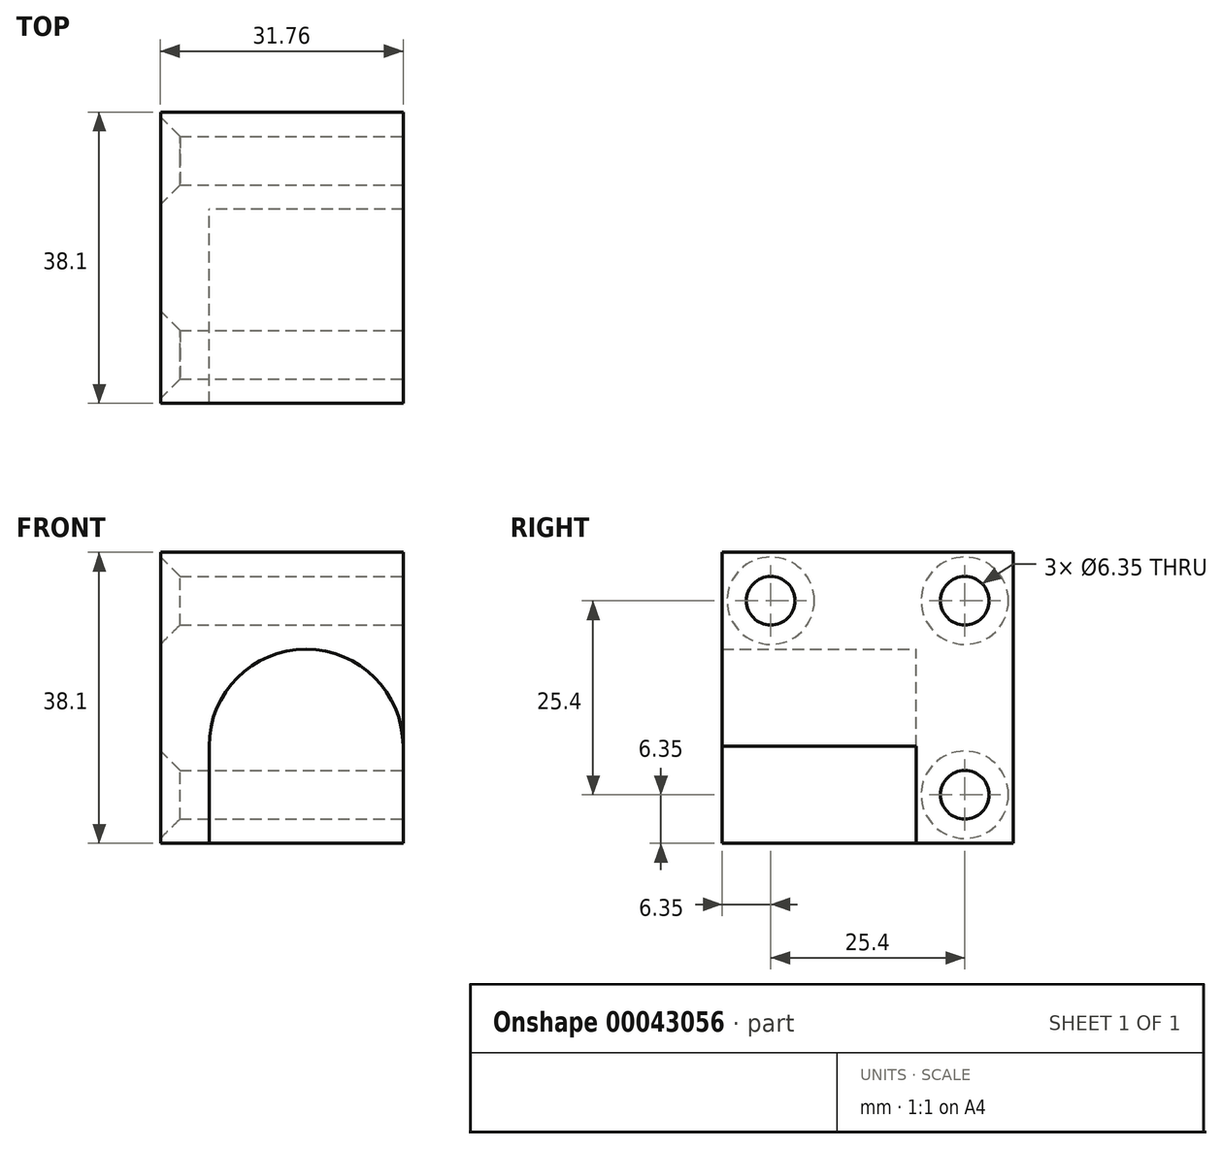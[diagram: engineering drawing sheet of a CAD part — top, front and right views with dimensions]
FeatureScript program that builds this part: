
annotation { "Feature Type Name" : "Feature", "Feature Type Description" : "" }
export const myFeature = defineFeature(function(context is Context, id is Id, definition is map)
    precondition{}
    {
        {
            var Q0;
            Q0=qCreatedBy(makeId("Front.planeOp"),FACE);
            var sketch = newSketch(context, id + "F0", { "sketchPlane" : qUnion([Q0])});
            skLineSegment(sketch, "E0.rect.bottom", {"start": v(15.88, 19.05) * mm, "end": v(-15.87, 19.05) * mm});
            skLineSegment(sketch, "E0.rect.top", {"start": v(15.87, -19.05) * mm, "end": v(-15.88, -19.05) * mm});
            skLineSegment(sketch, "E0.rect.left", {"start": v(15.87, 19.05) * mm, "end": v(15.87, -19.05) * mm});
            skLineSegment(sketch, "E0.rect.right", {"start": v(-15.88, 19.05) * mm, "end": v(-15.88, -19.05) * mm});
            skPoint(sketch, "E0.rect.middle", {"position": v(0, 0) * mm});
            skCircle(sketch, "E1", {"center": v(3.17, -6.35) * mm, "radius": 12.7 * mm});
            skLineSegment(sketch, "E2", {"start": v(-9.53, -6.35) * mm, "end": v(-9.53, -19.05) * mm});
            skSolve(sketch);
        }
        {
            var Q0;
            {var subQ4=sQuery(id+"F0.wireOp",EDGE,"E0.rect.bottom");Q0=makeQuery(id+"F0.imprint","IMPRINT",FACE,{"disambiguationData":[TD([[makeQuery(id+"F0.imprint","IMPRINT",EDGE,{"derivedFrom":subQ4}),1.0]])]});}
            extrude(context, id + "F1", {"entities" : qUnion([Q0]), "depth" : 38.1 * mm});
        }
        {
            var Q0;
            {var subQ0=sQuery(id+"F0.wireOp",EDGE,"E1");var subQ3=makeQuery(id+"F0.imprint","INTERSECT",VERTEX,{"derivedFrom":[subQ0,sQuery(id+"F0.wireOp",EDGE,"E2")]});Q0=makeQuery(id+"F0.imprint","IMPRINT",FACE,{"disambiguationData":[TD([[makeQuery(id+"F0.imprint","IMPRINT",EDGE,{"disambiguationData":[TD([[subQ3,1.0]])],"derivedFrom":subQ0}),1.0]])]});}
            var Q1;
            {var subQ1=sQuery(id+"F0.wireOp",EDGE,"E0.rect.left");var subQ3=sQuery(id+"F0.wireOp",EDGE,"E0.rect.top");var subQ5=makeQuery(id+"F0.imprint","INTERSECT",VERTEX,{"derivedFrom":[subQ3,subQ1]});Q1=makeQuery(id+"F0.imprint","IMPRINT",FACE,{"disambiguationData":[TD([[makeQuery(id+"F0.imprint","IMPRINT",EDGE,{"disambiguationData":[TD([[subQ5,-1.0]])],"derivedFrom":subQ3}),-1.0]])]});}
            var Q2;
            {var subQ0=sQuery(id+"F0.wireOp",EDGE,"E2");Q2=makeQuery(id+"F0.imprint","IMPRINT",FACE,{"disambiguationData":[TD([[makeQuery(id+"F0.imprint","IMPRINT",EDGE,{"derivedFrom":subQ0}),1.0]])]});}
            extrude(context, id + "F2", {"entities" : qUnion([Q0, Q1, Q2]), "operationType" : NewBodyOperationType.ADD, "depth" : 12.7 * mm});
        }
        {
            var Q0;
            {var subQ0=sQuery(id+"F0.wireOp",EDGE,"E0.rect.left");Q0=makeQuery(id+"F2.boolean.opBoolean","MERGE",FACE,{"derivedFrom":[makeQuery(id+"F1.opExtrude","SWEPT_FACE",FACE,{"disambiguationData":[OSD([subQ0])]}),makeQuery(id+"F2.opExtrude","SWEPT_FACE",FACE,{"disambiguationData":[OSD([subQ0])]})]});}
            var sketch = newSketch(context, id + "F3", { "sketchPlane" : qUnion([Q0])});
            skCircle(sketch, "E3", {"center": v(-31.75, 12.7) * mm, "radius": 3.18 * mm});
            skCircle(sketch, "E4", {"center": v(-6.35, 12.7) * mm, "radius": 3.18 * mm});
            skCircle(sketch, "E5", {"center": v(-6.35, -12.7) * mm, "radius": 3.18 * mm});
            skText(sketch, "E6", { "text": " mate to door", "fontName": "OpenSans-Bold.ttf"});
            const initialGuessF3  = {"E6": [-0.0381, 0.00241, 1, 0, 0.00394]};
            skSetInitialGuess(sketch, initialGuessF3);
            skSolve(sketch);
        }
        {
            var Q0;
            Q0=makeQuery(id+"F3.imprint","IMPRINT",FACE,{"disambiguationData":[TD([[makeQuery(id+"F3.imprint","IMPRINT",EDGE,{"derivedFrom":sQuery(id+"F3.wireOp",EDGE,"E3")}),1.0]])]});
            var Q1;
            Q1=makeQuery(id+"F3.imprint","IMPRINT",FACE,{"disambiguationData":[TD([[makeQuery(id+"F3.imprint","IMPRINT",EDGE,{"derivedFrom":sQuery(id+"F3.wireOp",EDGE,"E4")}),1.0]])]});
            var Q2;
            Q2=makeQuery(id+"F3.imprint","IMPRINT",FACE,{"disambiguationData":[TD([[makeQuery(id+"F3.imprint","IMPRINT",EDGE,{"derivedFrom":sQuery(id+"F3.wireOp",EDGE,"E5")}),1.0]])]});
            extrude(context, id + "F4", {"entities" : qUnion([Q0, Q1, Q2]), "operationType" : NewBodyOperationType.REMOVE, "endBound" : BoundingType.THROUGH_ALL, "oppositeDirection" : true, "depth" : 25.4 * mm});
        }
        {
            var Q0;
            Q0=makeQuery(id+"F4.boolean.opBoolean","INTERSECT",EDGE,{"derivedFrom":[makeQuery(id+"F1.opExtrude","SWEPT_FACE",FACE,{"disambiguationData":[OSD([sQuery(id+"F0.wireOp",EDGE,"E0.rect.right")])]}),makeQuery(id+"F4.opExtrude","SWEPT_FACE",FACE,{"disambiguationData":[OSD([sQuery(id+"F3.wireOp",EDGE,"E5")])]})]});
            var Q1;
            Q1=makeQuery(id+"F4.boolean.opBoolean","INTERSECT",EDGE,{"derivedFrom":[makeQuery(id+"F1.opExtrude","SWEPT_FACE",FACE,{"disambiguationData":[OSD([sQuery(id+"F0.wireOp",EDGE,"E0.rect.right")])]}),makeQuery(id+"F4.opExtrude","SWEPT_FACE",FACE,{"disambiguationData":[OSD([sQuery(id+"F3.wireOp",EDGE,"E4")])]})]});
            var Q2;
            Q2=makeQuery(id+"F4.boolean.opBoolean","INTERSECT",EDGE,{"derivedFrom":[makeQuery(id+"F1.opExtrude","SWEPT_FACE",FACE,{"disambiguationData":[OSD([sQuery(id+"F0.wireOp",EDGE,"E0.rect.right")])]}),makeQuery(id+"F4.opExtrude","SWEPT_FACE",FACE,{"disambiguationData":[OSD([sQuery(id+"F3.wireOp",EDGE,"E3")])]})]});
            chamfer(context, id + "F5", {"entities" : qUnion([Q0, Q1, Q2]), "width" : 2.54 * mm, "tangentPropagation" : true});
        }
    });
